# Revit family: GO_undercabinet 450
name_source: partatom
category: Furniture
units: mm (PartAtom-declared; Revit-internal decimal feet)

## family parameters
Always vertical = Yes
Cut with Voids When Loaded = No
OmniClass Number = 23.40.20.00
OmniClass Title = General Furniture and Specialties
Room Calculation Point = No
Shared = No
Work Plane-Based = No

## types (3) — shared parameters
Depth = 294 mm  [stored 0.964567 ft]
ETIM = EC011382
Manufacturer = Hafa Bathroom Group AB
Material body = Moisture resistant chip board E1 certified
Material front = Moisure resistant MDF FSC and  E1 certified
Model = Go under cabinets
Surface finish = Lacquered
Svulsthöjd = 550 mm  [stored 1.80446 ft]
URL = www.hafa.se
Width = 430 mm  [stored 1.41076 ft]

## per-type parameters (varying)
| type | Article number | Finish | GTIN |
| Go 450 white matt | 1580000 | NCS S 0300-N 20% gloss white matt | 7330027103518 |
| Go 450 black matt | 1580001 | NCS S 9000-N 10% gloss black matt | 7330027103525 |
| Go 450 white high gloss | 1580002 | NCS S 0300-N 90% gloss white highgloss | 7330027096810 |

note: [stored X ft] marks values corroborated as IEEE doubles in the binary element streams (Revit-internal decimal feet)

## geometry (parser evidence)
native form markers: Sweep x7
no freeform markers — native parametric forms only
